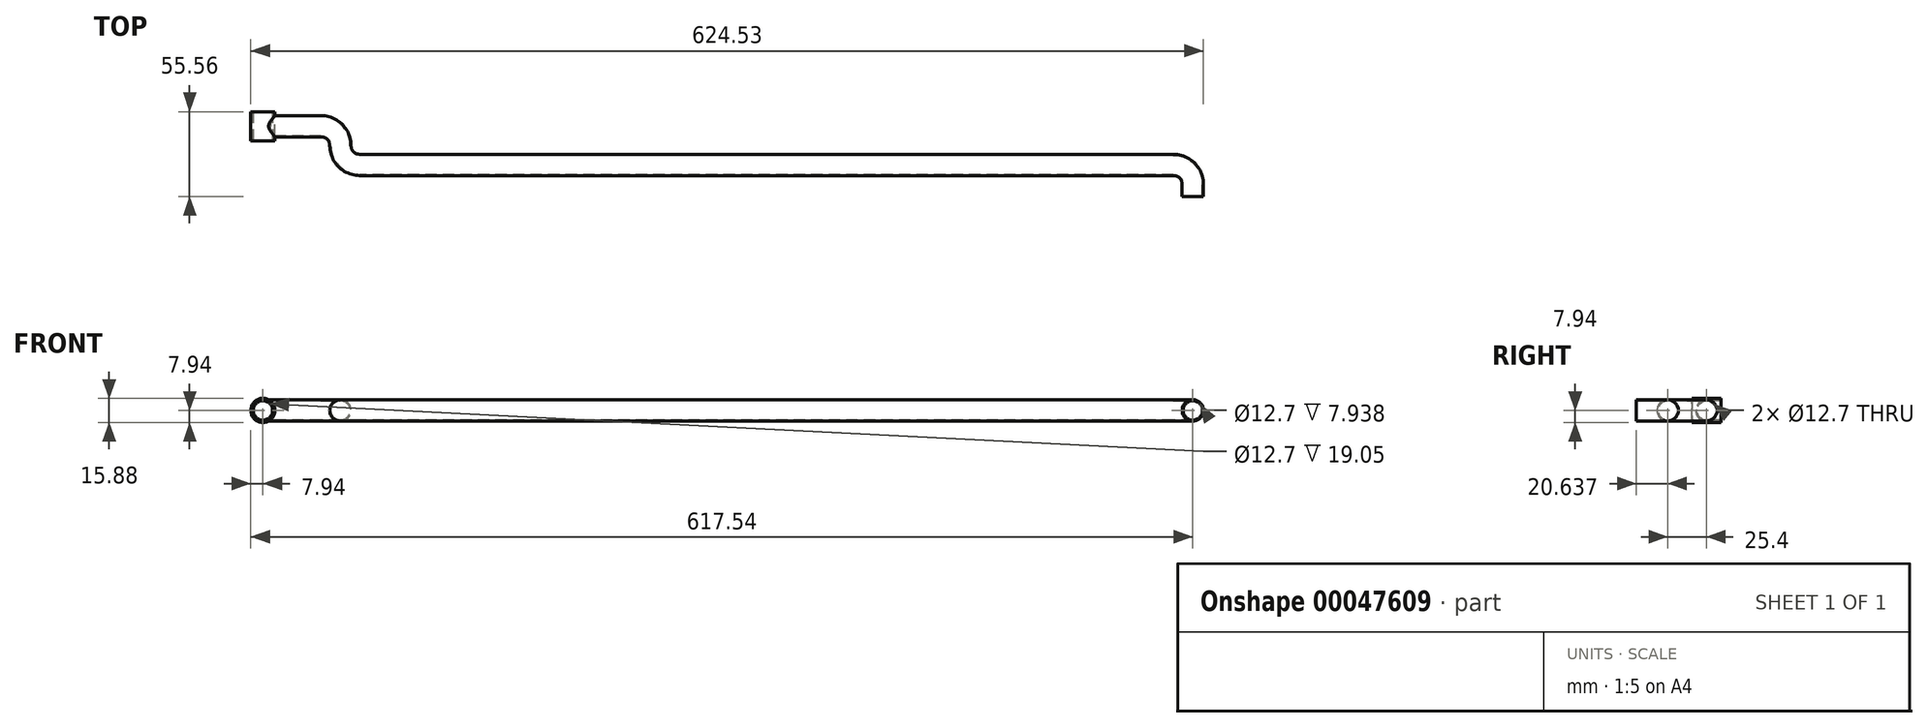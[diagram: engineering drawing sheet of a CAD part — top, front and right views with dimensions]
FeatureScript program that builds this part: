
annotation { "Feature Type Name" : "Feature", "Feature Type Description" : "" }
export const myFeature = defineFeature(function(context is Context, id is Id, definition is map)
    precondition{}
    {
        {
            var Q0;
            Q0=qCreatedBy(makeId("Front.planeOp"),FACE);
            var sketch = newSketch(context, id + "F0", { "sketchPlane" : qUnion([Q0])});
            skCircle(sketch, "E0", {"center": v(0, 0) * mm, "radius": 6.99 * mm});
            skCircle(sketch, "E1", {"center": v(0, 0) * mm, "radius": 6.35 * mm});
            skSolve(sketch);
        }
        {
            var Q0;
            Q0=qCreatedBy(makeId("Top.planeOp"),FACE);
            var sketch = newSketch(context, id + "F1", { "sketchPlane" : qUnion([Q0])});
            skLineSegment(sketch, "E2", {"start": v(0, 0) * mm, "end": v(0, 7.94) * mm});
            skLineSegment(sketch, "E3", {"start": v(-12.7, 20.64) * mm, "end": v(-546.1, 20.64) * mm});
            skPoint(sketch, "E4.visualSharp", {"position": v(0, 20.64) * mm});
            skArc(sketch, "E4.filletArc", {"start": v(0, 7.94) * mm, "mid": v(-3.72, 16.92) * mm, "end": v(-12.7, 20.64) * mm});
            skLineSegment(sketch, "E5", {"start": v(-558.8, 33.34) * mm, "end": v(-558.8, 33.34) * mm});
            skLineSegment(sketch, "E6", {"start": v(-571.5, 46.04) * mm, "end": v(-609.6, 46.04) * mm});
            skPoint(sketch, "E7.visualSharp", {"position": v(-558.8, 20.64) * mm});
            skArc(sketch, "E7.filletArc", {"start": v(-558.8, 33.34) * mm, "mid": v(-555.08, 24.36) * mm, "end": v(-546.1, 20.64) * mm});
            skPoint(sketch, "E8.visualSharp", {"position": v(-558.8, 46.04) * mm});
            skArc(sketch, "E8.filletArc", {"start": v(-558.8, 33.34) * mm, "mid": v(-562.52, 42.32) * mm, "end": v(-571.5, 46.04) * mm});
            skSolve(sketch);
        }
        {
            var Q0;
            Q0 = qSketchRegion(id + "F0", true);
            var Q1;
            Q1 = qConstructionFilter(qBodyType(qCreatedBy(id + "F1" ,EDGE), BodyType.WIRE), ConstructionObject.NO);
            sweep(context, id + "F2", {"profiles" : qUnion([Q0]), "path" : qUnion([Q1])});
        }
        {
            var Q0;
            Q0=qCreatedBy(makeId("Front.planeOp"),FACE);
            cPlane(context, id + "F3", {"entities" : qUnion([Q0]), "cplaneType" : CPlaneType.OFFSET, "offset" : 46.04 * mm, "oppositeDirection" : true, "width" : 152.4 * mm, "height" : 152.4 * mm});
        }
        {
            var Q0;
            Q0=qCreatedBy(id+"F3.planeOp",FACE);
            var sketch = newSketch(context, id + "F4", { "sketchPlane" : qUnion([Q0])});
            skCircle(sketch, "E9", {"center": v(-609.6, 0) * mm, "radius": 7.94 * mm});
            skSolve(sketch);
        }
        {
            var Q0;
            Q0 = qSketchRegion(id + "F4", true);
            extrude(context, id + "F5", {"entities" : qUnion([Q0]), "operationType" : NewBodyOperationType.ADD, "depth" : 19.05 * mm, "symmetric" : true});
        }
        {
            var Q0;
            Q0=makeQuery(id+"F5.opExtrude","CAP_FACE",FACE,{"disambiguationData":[OSD([sQuery(id+"F4.wireOp",EDGE,"E9")])],"isStart":false});
            var sketch = newSketch(context, id + "F6", { "sketchPlane" : qUnion([Q0])});
            skCircle(sketch, "E10", {"center": v(-609.6, 0) * mm, "radius": 6.35 * mm});
            skSolve(sketch);
        }
        {
            var Q0;
            Q0 = qSketchRegion(id + "F6", true);
            var Q1;
            Q1=makeQuery(id+"F5.opExtrude","CAP_FACE",FACE,{"disambiguationData":[OSD([sQuery(id+"F4.wireOp",EDGE,"E9")])],"isStart":true});
            extrude(context, id + "F7", {"entities" : qUnion([Q0]), "operationType" : NewBodyOperationType.REMOVE, "endBound" : BoundingType.UP_TO_SURFACE, "oppositeDirection" : true, "endBoundEntityFace" : qUnion([Q1]), "depth" : 25.4 * mm});
        }
    });
